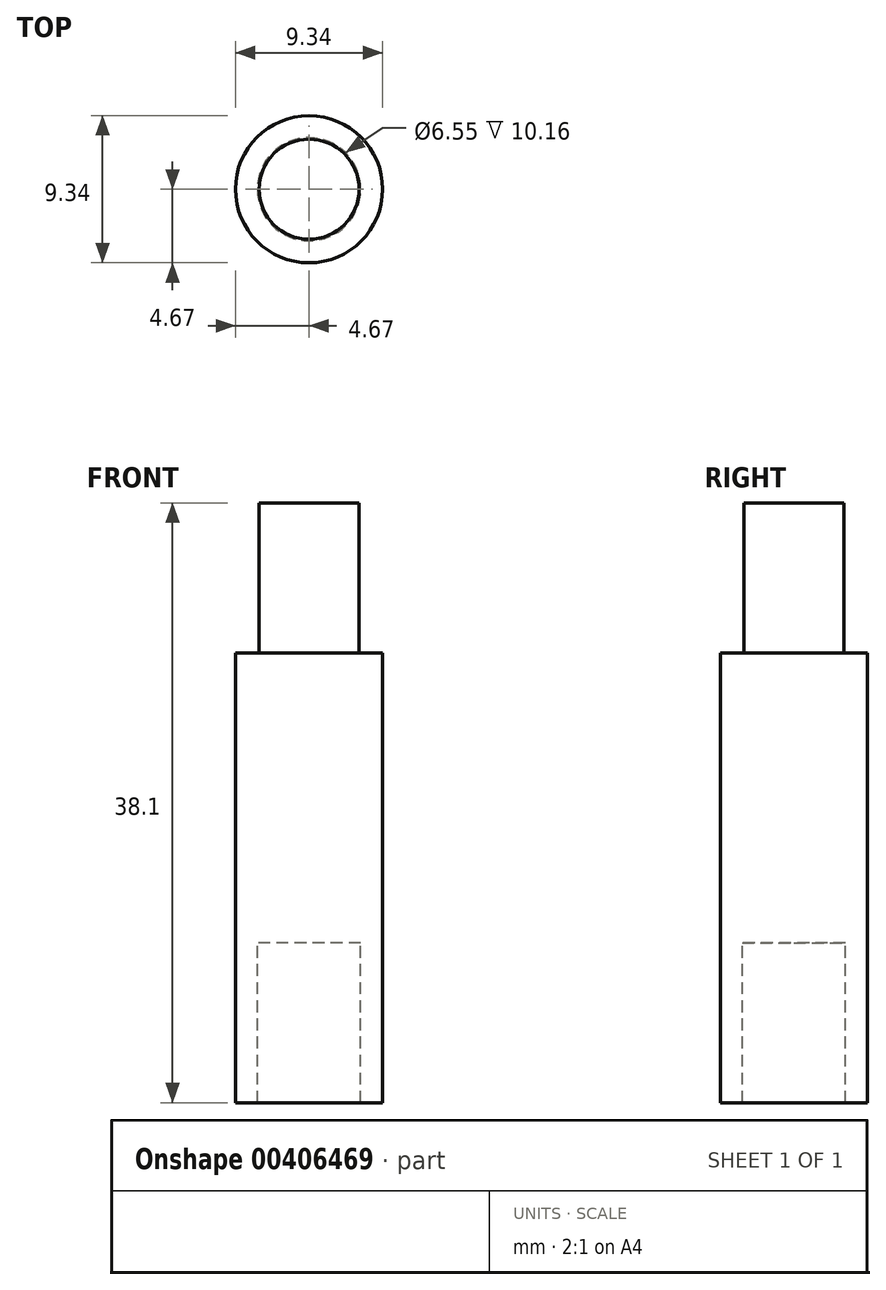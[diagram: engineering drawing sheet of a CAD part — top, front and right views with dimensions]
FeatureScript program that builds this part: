
annotation { "Feature Type Name" : "Feature", "Feature Type Description" : "" }
export const myFeature = defineFeature(function(context is Context, id is Id, definition is map)
    precondition{}
    {
        {
            var Q0;
            Q0=qCreatedBy(makeId("Front.planeOp"),FACE);
            var sketch = newSketch(context, id + "F0", { "sketchPlane" : qUnion([Q0])});
            skLineSegment(sketch, "E0", {"start": v(0, 10.16) * mm, "end": v(3.28, 10.16) * mm});
            skLineSegment(sketch, "E1", {"start": v(3.28, 10.16) * mm, "end": v(3.28, 0) * mm});
            skLineSegment(sketch, "E2", {"start": v(3.28, 0) * mm, "end": v(4.67, 0) * mm});
            skLineSegment(sketch, "E3", {"start": v(4.67, 0) * mm, "end": v(4.67, 28.58) * mm});
            skLineSegment(sketch, "E4", {"start": v(4.67, 28.58) * mm, "end": v(3.18, 28.58) * mm});
            skLineSegment(sketch, "E5", {"start": v(3.18, 28.58) * mm, "end": v(3.18, 38.1) * mm});
            skLineSegment(sketch, "E6", {"start": v(3.18, 38.1) * mm, "end": v(0, 38.1) * mm});
            skLineSegment(sketch, "E7", {"start": v(0, 38.1) * mm, "end": v(0, 10.16) * mm});
            skSolve(sketch);
        }
        {
            var Q0;
            Q0=makeQuery(id+"F0.imprint","IMPRINT",FACE,{"disambiguationData":[TD([[makeQuery(id+"F0.imprint","IMPRINT",EDGE,{"derivedFrom":sQuery(id+"F0.wireOp",EDGE,"E0")}),1.0]])]});
            var Q1;
            Q1=sQuery(id+"F0.wireOp",EDGE,"E7");
            revolve(context, id + "F1", {"entities" : qUnion([Q0]), "axis" : qUnion([Q1]), "revolveType" : RevolveType.FULL});
        }
    });
